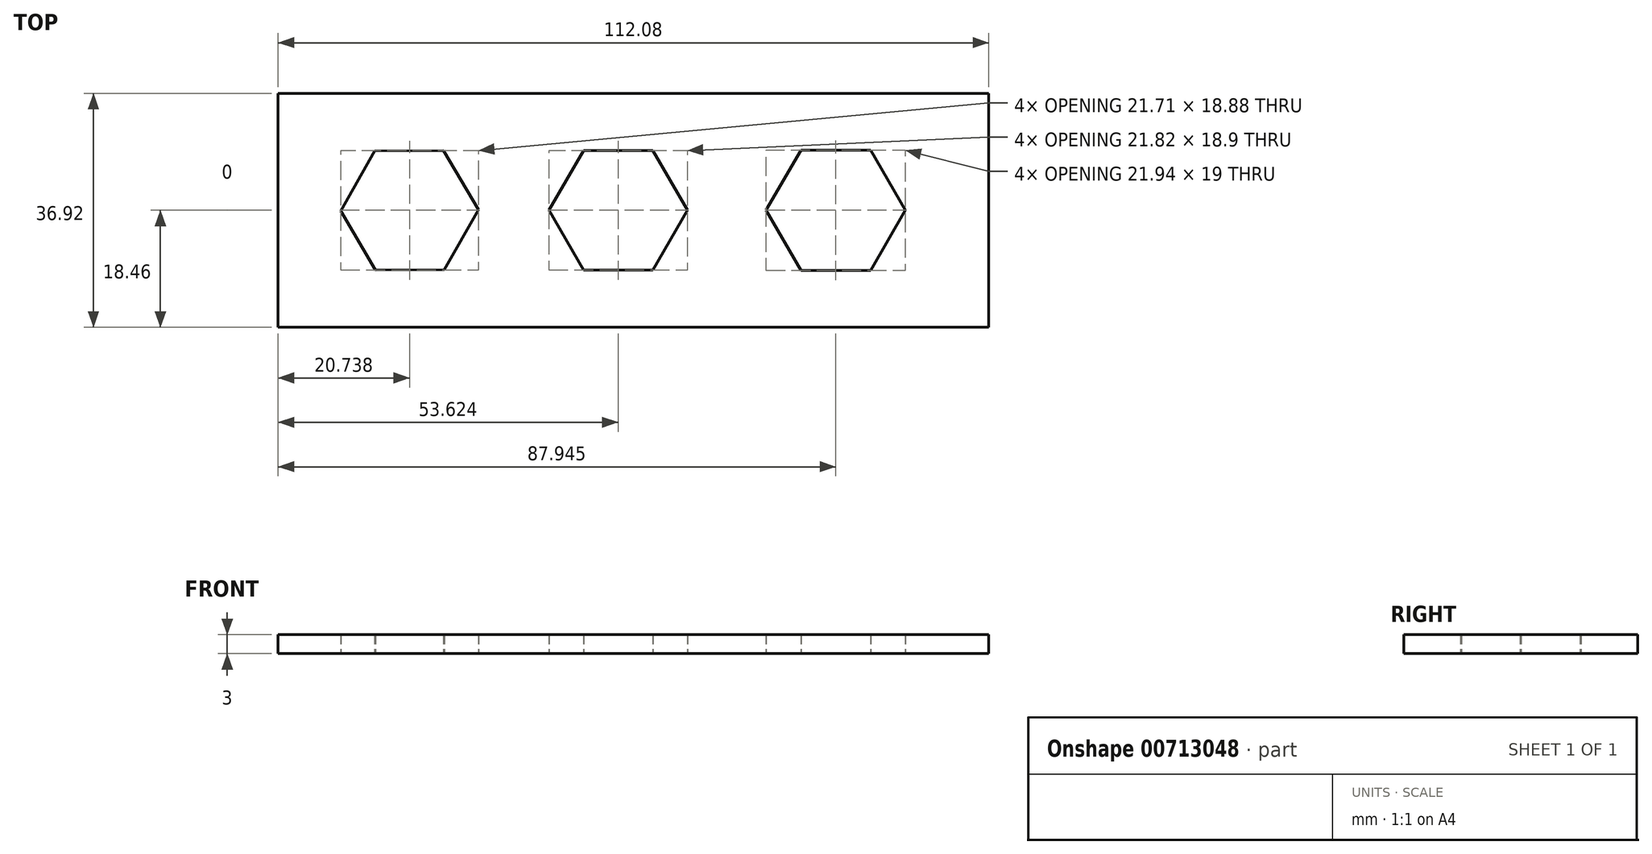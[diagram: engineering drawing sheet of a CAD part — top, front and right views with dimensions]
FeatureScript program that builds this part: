
annotation { "Feature Type Name" : "Feature", "Feature Type Description" : "" }
export const myFeature = defineFeature(function(context is Context, id is Id, definition is map)
    precondition{}
    {
        {
            var Q0;
            Q0=qCreatedBy(makeId("Top.planeOp"),FACE);
            var sketch = newSketch(context, id + "F0", { "sketchPlane" : qUnion([Q0])});
            skLineSegment(sketch, "E0.bottom", {"start": v(-56.04, 18.46) * mm, "end": v(56.04, 18.46) * mm});
            skLineSegment(sketch, "E0.top", {"start": v(-56.04, -18.46) * mm, "end": v(56.04, -18.46) * mm});
            skLineSegment(sketch, "E0.left", {"start": v(-56.04, 18.46) * mm, "end": v(-56.04, -18.46) * mm});
            skLineSegment(sketch, "E0.right", {"start": v(56.04, 18.46) * mm, "end": v(56.04, -18.46) * mm});
            skLineSegment(sketch, "E1.bottom", {"start": v(0, -18.46) * mm, "end": v(0, -18.46) * mm});
            skLineSegment(sketch, "E1.top", {"start": v(0, 18.46) * mm, "end": v(0, 18.46) * mm});
            skLineSegment(sketch, "E2", {"start": v(0, 18.46) * mm, "end": v(0, -18.46) * mm, "construction": true});
            skLineSegment(sketch, "E3", {"start": v(56.04, 0) * mm, "end": v(-56.04, 0) * mm, "construction": true});
            skCircle(sketch, "E4.cCircle", {"center": v(-35.3, 0) * mm, "radius": 9.4 * mm, "construction": true});
            skLineSegment(sketch, "E4.0", {"start": v(-29.94, 9.44) * mm, "end": v(-24.45, 0.08) * mm});
            skLineSegment(sketch, "E4.1", {"start": v(-24.45, 0.08) * mm, "end": v(-29.8, -9.36) * mm});
            skLineSegment(sketch, "E4.2", {"start": v(-29.8, -9.36) * mm, "end": v(-40.66, -9.44) * mm});
            skLineSegment(sketch, "E4.3", {"start": v(-40.66, -9.44) * mm, "end": v(-46.16, -0.08) * mm});
            skLineSegment(sketch, "E4.4", {"start": v(-46.16, -0.08) * mm, "end": v(-40.8, 9.36) * mm});
            skLineSegment(sketch, "E4.5", {"start": v(-40.8, 9.36) * mm, "end": v(-29.94, 9.44) * mm});
            skPoint(sketch, "E4.0.midPoint", {"position": v(-27.2, 4.76) * mm});
            skCircle(sketch, "E5.cCircle", {"center": v(-2.42, 0) * mm, "radius": 9.45 * mm, "construction": true});
            skLineSegment(sketch, "E5.0", {"start": v(3.04, -9.45) * mm, "end": v(-7.87, -9.45) * mm});
            skLineSegment(sketch, "E5.1", {"start": v(-7.87, -9.45) * mm, "end": v(-13.33, 0) * mm});
            skLineSegment(sketch, "E5.2", {"start": v(-13.33, 0) * mm, "end": v(-7.87, 9.45) * mm});
            skLineSegment(sketch, "E5.3", {"start": v(-7.87, 9.45) * mm, "end": v(3.04, 9.45) * mm});
            skLineSegment(sketch, "E5.4", {"start": v(3.04, 9.45) * mm, "end": v(8.5, 0) * mm});
            skLineSegment(sketch, "E5.5", {"start": v(8.5, 0) * mm, "end": v(3.04, -9.45) * mm});
            skPoint(sketch, "E5.0.midPoint", {"position": v(-2.42, -9.45) * mm});
            skCircle(sketch, "E6.cCircle", {"center": v(31.9, 0) * mm, "radius": 9.5 * mm, "construction": true});
            skLineSegment(sketch, "E6.0", {"start": v(37.4, -9.5) * mm, "end": v(26.42, -9.5) * mm});
            skLineSegment(sketch, "E6.1", {"start": v(26.42, -9.5) * mm, "end": v(20.94, 0) * mm});
            skLineSegment(sketch, "E6.2", {"start": v(20.94, 0) * mm, "end": v(26.42, 9.5) * mm});
            skLineSegment(sketch, "E6.3", {"start": v(26.42, 9.5) * mm, "end": v(37.4, 9.5) * mm});
            skLineSegment(sketch, "E6.4", {"start": v(37.4, 9.5) * mm, "end": v(42.88, 0) * mm});
            skLineSegment(sketch, "E6.5", {"start": v(42.88, 0) * mm, "end": v(37.4, -9.5) * mm});
            skPoint(sketch, "E6.0.midPoint", {"position": v(31.9, -9.5) * mm});
            skSolve(sketch);
        }
        {
            var Q0;
            Q0=makeQuery(id+"F0.imprint","IMPRINT",FACE,{"disambiguationData":[TD([[makeQuery(id+"F0.imprint","IMPRINT",EDGE,{"derivedFrom":sQuery(id+"F0.wireOp",EDGE,"E0.bottom")}),-1.0]])]});
            extrude(context, id + "F1", {"entities" : qUnion([Q0]), "depth" : 3 * mm, "offsetDistance" : 25 * mm});
        }
    });
